# Revit family: PT,PS, 69, 99, 612, 912, 615, 68
name_source: partatom
category: Windows
revit_build: Autodesk Revit LT 2016 (Build: 20150220_1215(x64)
units: mm (PartAtom-declared; Revit-internal decimal feet)

## family parameters
Always vertical = Yes
Cut with Voids When Loaded = No
Host = Wall
OmniClass Number = 23.30.20.00
OmniClass Title = Windows
Room Calculation Point = No
Shared = No

## types (6) — shared parameters
Aluminium anodized = Aluminium
Bottom guide = 33 mm
Default Sill Height = 914 mm
Glazing = Glass
Manufacturer = Robmeg
Plaster = 5 mm  [stored 0.0164042 ft]
Rough Height = 1219 mm
URL = http://www.robmeg.co.za
Wall Closure = By host

## per-type parameters (varying)
| type | Bottom glass thickness | Description | Height | Model | Mullion height | Side hung | Top hung | Width |
| PT Type- 69 | 4 mm  [stored 0.0131234 ft] | Anodized Aluminium | 910 mm  [stored 2.98556 ft] | PT 69 | 200 mm  [stored 0.656168 ft] | No | Yes | 610 mm  [stored 2.00131 ft] |
| PT Type-  99 | 4 mm  [stored 0.0131234 ft] | Anodized Aluminium | 910 mm  [stored 2.98556 ft] | PT 99 | 200 mm  [stored 0.656168 ft] | No | Yes | 910 mm  [stored 2.98556 ft] |
| PT Type- 612 | 4 mm  [stored 0.0131234 ft] | Anodized Aluminium | 1210 mm  [stored 3.96982 ft] | PT 612 | 600 mm | No | Yes | 610 mm  [stored 2.00131 ft] |
| PT Type- 912 | 4 mm  [stored 0.0131234 ft] | Anodized Aluminium | 1210 mm  [stored 3.96982 ft] | PT 912 | 600 mm | No | Yes | 910 mm  [stored 2.98556 ft] |
| PS Type- 615 | 4 mm  [stored 0.0131234 ft] | Anodized Alumium | 1510 mm  [stored 4.95407 ft] | PS 615 | 375 mm  [stored 1.23031 ft] | Yes | No | 610 mm  [stored 2.00131 ft] |
| PS Type- 618 | 6 mm  [stored 0.019685 ft] | Anodized Aluminum | 1510 mm  [stored 4.95407 ft] | PS 618 | 500 mm  [stored 1.64042 ft] | Yes | No | 610 mm  [stored 2.00131 ft] |

note: [stored X ft] marks values corroborated as IEEE doubles in the binary element streams (Revit-internal decimal feet)

## geometry (parser evidence)
native form markers: Sweep x3
no freeform markers — native parametric forms only
